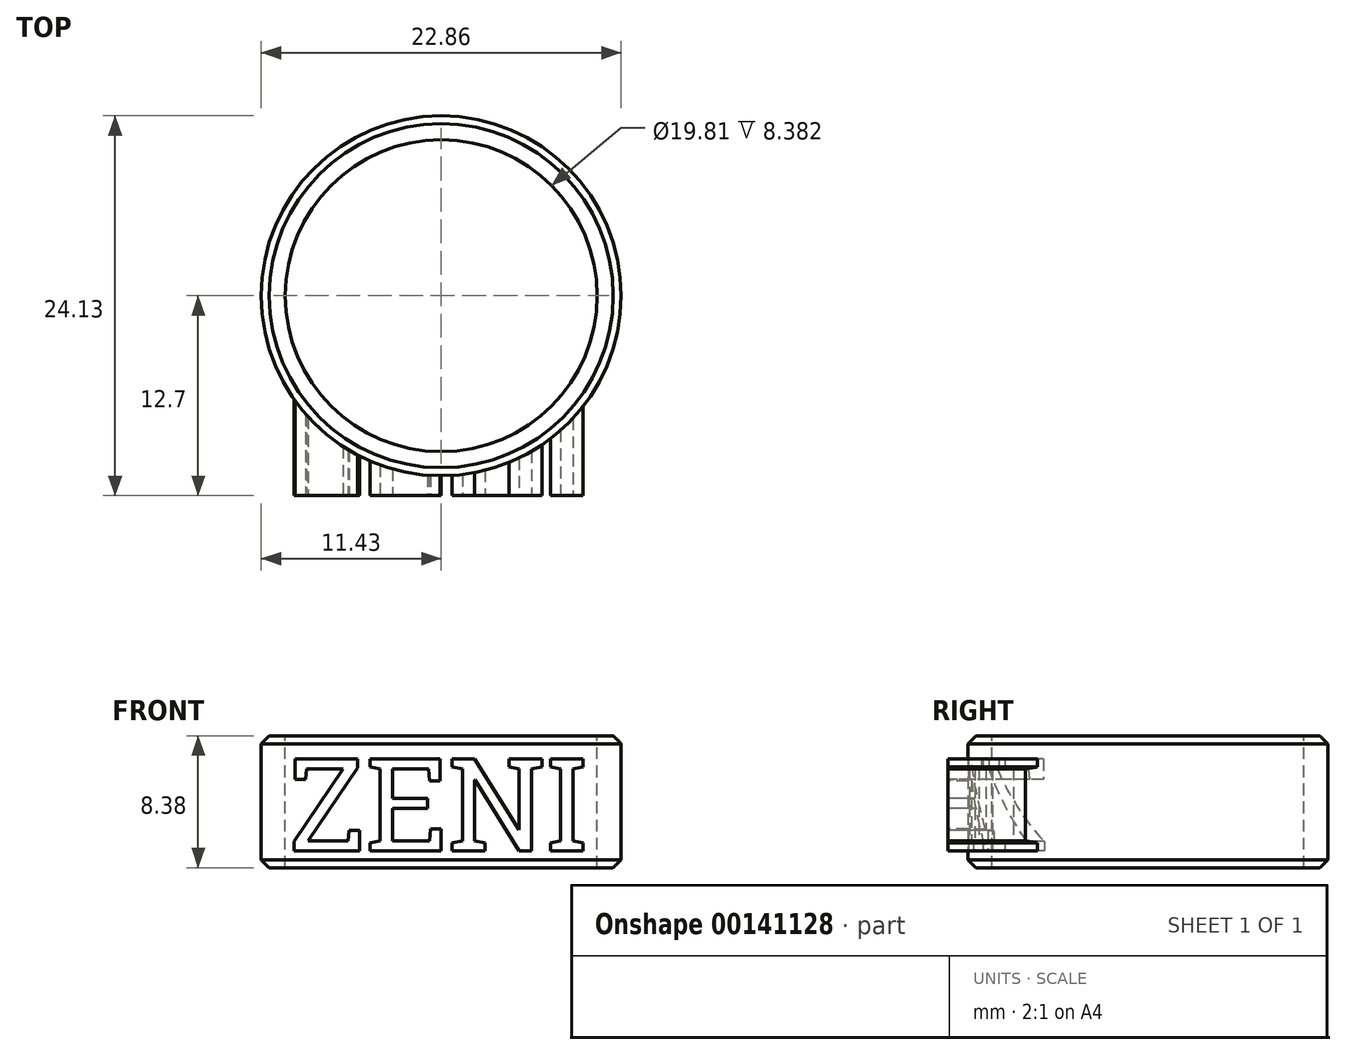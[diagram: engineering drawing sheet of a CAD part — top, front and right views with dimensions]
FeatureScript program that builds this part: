
annotation { "Feature Type Name" : "Feature", "Feature Type Description" : "" }
export const myFeature = defineFeature(function(context is Context, id is Id, definition is map)
    precondition{}
    {
        {
            var Q0;
            Q0=qCreatedBy(makeId("Top.planeOp"),FACE);
            var sketch = newSketch(context, id + "F0", { "sketchPlane" : qUnion([Q0])});
            skCircle(sketch, "E0", {"center": v(0, 0) * mm, "radius": 11.43 * mm});
            skSolve(sketch);
        }
        {
            var Q0;
            Q0=makeQuery(id+"F0.imprint","IMPRINT",FACE,{"disambiguationData":[TD([[makeQuery(id+"F0.imprint","IMPRINT",EDGE,{"derivedFrom":sQuery(id+"F0.wireOp",EDGE,"E0")}),1.0]])]});
            extrude(context, id + "F1", {"entities" : qUnion([Q0]), "depth" : 8.38 * mm});
        }
        {
            var Q0;
            Q0=makeQuery(id+"F1.opExtrude","CAP_FACE",FACE,{"disambiguationData":[OSD([sQuery(id+"F0.wireOp",EDGE,"E0")])],"isStart":false});
            var sketch = newSketch(context, id + "F2", { "sketchPlane" : qUnion([Q0])});
            skPoint(sketch, "E1", {"position": v(0, 0) * mm});
            skSolve(sketch);
        }
        {
            var Q0;
            Q0=sQuery(id+"F2.wireOp",VERTEX,"E1");
            var Q1;
            Q1=makeQuery(id+"F1.opExtrude","SWEPT_BODY",BODY,{"disambiguationData":[OSD([sQuery(id+"F0.wireOp",EDGE,"E0")])]});
            hole(context, id + "F3", {"style" : HoleStyle.SIMPLE, "endStyle" : HoleEndStyle.THROUGH, "holeDiameter" : 19.8 * mm, "startFromSketch" : true, "locations" : qUnion([Q0]), "scope" : qUnion([Q1]), "isTappedThrough" : true});
        }
        {
            var Q0;
            Q0=makeQuery(id+"F1.opExtrude","CAP_EDGE",EDGE,{"disambiguationData":[OSD([sQuery(id+"F0.wireOp",EDGE,"E0")])],"isStart":false});
            var Q1;
            Q1=makeQuery(id+"F3.hole-0.boolean.opBoolean","COPY",EDGE,{"derivedFrom":makeQuery(id+"F3.hole-0.opRevolve","SWEPT_EDGE",EDGE,{"disambiguationData":[OSD([sQuery(id+"F3.hole-0.sketch.wireOp",EDGE,"core_line_2"),sQuery(id+"F3.hole-0.sketch.wireOp",EDGE,"core_line_3")])]})});
            var Q2;
            Q2=makeQuery(id+"F1.opExtrude","CAP_EDGE",EDGE,{"disambiguationData":[OSD([sQuery(id+"F0.wireOp",EDGE,"E0")])],"isStart":true});
            var Q3;
            Q3=makeQuery(id+"F3.hole-0.boolean.opBoolean","INTERSECT",EDGE,{"derivedFrom":[makeQuery(id+"F1.opExtrude","CAP_FACE",FACE,{"disambiguationData":[OSD([sQuery(id+"F0.wireOp",EDGE,"E0")])],"isStart":true}),makeQuery(id+"F3.hole-0.opRevolve","SWEPT_FACE",FACE,{"disambiguationData":[OSD([sQuery(id+"F3.hole-0.sketch.wireOp",EDGE,"core_line_2")])]})]});
            chamfer(context, id + "F4", {"entities" : qUnion([Q0, Q1, Q2, Q3]), "width" : 0.5 * mm, "tangentPropagation" : true});
        }
        {
            var Q0;
            Q0=qCreatedBy(makeId("Front.planeOp"),FACE);
            cPlane(context, id + "F5", {"entities" : qUnion([Q0]), "cplaneType" : CPlaneType.OFFSET, "offset" : 12.7 * mm, "width" : 152.4 * mm, "height" : 152.4 * mm});
        }
        {
            var Q0;
            Q0=qCreatedBy(id+"F5.planeOp",FACE);
            var sketch = newSketch(context, id + "F6", { "sketchPlane" : qUnion([Q0])});
            skText(sketch, "E2", { "text": "ZENI", "fontName": "RobotoSlab-Regular.ttf"});
            const initialGuessF6  = {"E2": [-0.0097, 0.00108, 1, 0, 0.0059]};
            skSetInitialGuess(sketch, initialGuessF6);
            skSolve(sketch);
        }
        {
            var Q0;
            Q0 = qSketchRegion(id + "F6", true);
            extrude(context, id + "F7", {"entities" : qUnion([Q0]), "operationType" : NewBodyOperationType.ADD, "endBound" : BoundingType.UP_TO_NEXT, "oppositeDirection" : true, "depth" : 25.4 * mm});
        }
    });
